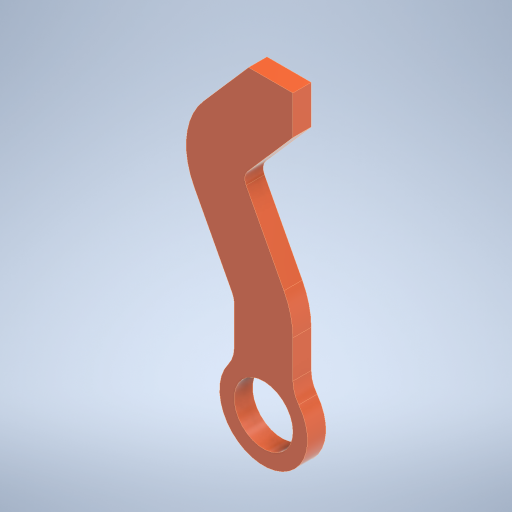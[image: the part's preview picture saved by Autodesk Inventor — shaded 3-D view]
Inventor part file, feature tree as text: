
AUTODESK INVENTOR PART (.ipt)
format: ipt  version: 2023.2 (Build 272271000, 271)  size: 279,040 bytes
history: native  units: mm
features: extrude x1, sketch x1
ambient origin geometry x8: Origin, YZ Plane, XZ Plane, XY Plane, X Axis, Y Axis, Z Axis, Center Point
bodies: Solid1 (feature_tree)
feature tree (2):
  extrude  "Extrusion1"  Depth=2.5mm TaperAngle=0.0deg
  sketch  "Sketch1"  dims[d1=8.0mm d2=2.5mm d3=0.0mm d4=12.0mm d5=30.0deg d6=19.198622mm d7=12.0mm d8=0.0mm d9=10.0mm d12=8.0mm d16=8.0mm d17=8.0mm d18=25.0mm d19=4.0mm d20=2.0mm d21=2.800309mm d22=13.393556mm d23=1.979367mm d24=28.288784mm d25=0.0mm]
